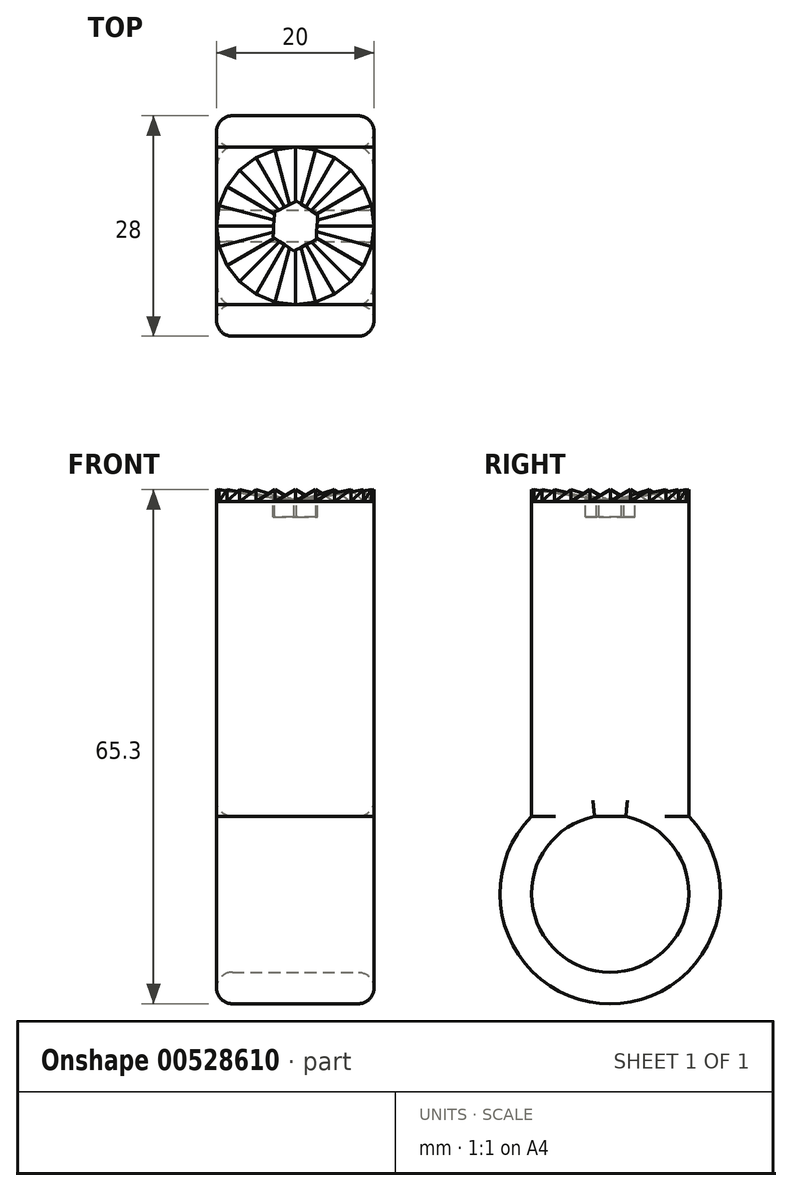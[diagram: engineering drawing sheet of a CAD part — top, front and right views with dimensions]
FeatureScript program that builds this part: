
annotation { "Feature Type Name" : "Feature", "Feature Type Description" : "" }
export const myFeature = defineFeature(function(context is Context, id is Id, definition is map)
    precondition{}
    {
        {
            var Q0;
            Q0=qCreatedBy(makeId("Top.planeOp"),FACE);
            var sketch = newSketch(context, id + "F0", { "sketchPlane" : qUnion([Q0])});
            skCircle(sketch, "E0", {"center": v(0, 0) * mm, "radius": 10 * mm});
            skLineSegment(sketch, "E1", {"start": v(0, 0) * mm, "end": v(0, 10) * mm});
            skLineSegment(sketch, "E2", {"start": v(0, 0) * mm, "end": v(2.59, 9.66) * mm});
            skLineSegment(sketch, "E3", {"start": v(0, 10) * mm, "end": v(2.59, 9.66) * mm});
            skCircle(sketch, "E4", {"center": v(0, 0) * mm, "radius": 1.5 * mm});
            skSolve(sketch);
        }
        {
            var Q0;
            Q0=sQuery(id+"F0.wireOp",EDGE,"E3");
            cPlane(context, id + "F1", {"entities" : qUnion([Q0]), "cplaneType" : CPlaneType.LINE_ANGLE, "offset" : 25 * mm, "angle" : 0 * degree, "width" : 150 * mm, "height" : 150 * mm});
        }
        {
            var Q0;
            Q0=qCreatedBy(id+"F1.planeOp",FACE);
            var sketch = newSketch(context, id + "F2", { "sketchPlane" : qUnion([Q0])});
            skLineSegment(sketch, "E5", {"start": v(1.3, 0) * mm, "end": v(1.3, 1.5) * mm});
            skLineSegment(sketch, "E6", {"start": v(1.3, 1.5) * mm, "end": v(-1.3, 0) * mm});
            skLineSegment(sketch, "E7", {"start": v(-1.3, 0) * mm, "end": v(1.3, 0) * mm});
            skLineSegment(sketch, "E8", {"start": v(-1.3, 0) * mm, "end": v(-1.3, 1.5) * mm});
            skLineSegment(sketch, "E9", {"start": v(-1.3, 1.5) * mm, "end": v(1.3, 1.5) * mm});
            skSolve(sketch);
        }
        {
            var Q0;
            Q0=makeQuery(id+"F2.imprint","IMPRINT",FACE,{"disambiguationData":[TD([[makeQuery(id+"F2.imprint","IMPRINT",EDGE,{"derivedFrom":sQuery(id+"F2.wireOp",EDGE,"E5")}),1.0]])]});
            var Q1;
            Q1=sQuery(id+"F0.wireOp",VERTEX,"E0.center");
            loft(context, id + "F3", {"sheetProfilesArray" : [{ "sheetProfileEntities" : qUnion([Q0]) }, { "sheetProfileEntities" : qUnion([Q1]) }]});
        }
        {
            var Q0;
            Q0=qCreatedBy(makeId("Right.planeOp"),FACE);
            var sketch = newSketch(context, id + "F4", { "sketchPlane" : qUnion([Q0])});
            skLineSegment(sketch, "E10", {"start": v(0, -4.83) * mm, "end": v(0, 8.7) * mm, "construction": true});
            skSolve(sketch);
        }
        {
            var Q0;
            Q0=makeQuery(id+"F3.opLoft","SWEPT_BODY",BODY,{"disambiguationData":[OSD([sQuery(id+"F0.wireOp",VERTEX,"E0.center"),makeQuery(id+"F2.imprint","IMPRINT",FACE,{"disambiguationData":[TD([[makeQuery(id+"F2.imprint","IMPRINT",EDGE,{"derivedFrom":sQuery(id+"F2.wireOp",EDGE,"E5")}),1.0]])]})])]});
            var Q1;
            Q1=sQuery(id+"F4.wireOp",EDGE,"E10");
            circularPattern(context, id + "F5", {"entities" : qUnion([Q0]), "axis" : qUnion([Q1]), "angle" : 360 * degree, "instanceCount" : 24, "equalSpace" : true});
        }
        {
            var Q0;
            Q0=qCreatedBy(makeId("Right.planeOp"),FACE);
            var sketch = newSketch(context, id + "F6", { "sketchPlane" : qUnion([Q0])});
            skLineSegment(sketch, "E11", {"start": v(0, 0) * mm, "end": v(-10, 0) * mm, "construction": true});
            skLineSegment(sketch, "E12.bottom", {"start": v(-10, 0) * mm, "end": v(10, 0) * mm});
            skLineSegment(sketch, "E12.top", {"start": v(-10, -40) * mm, "end": v(10, -40) * mm});
            skLineSegment(sketch, "E12.left", {"start": v(-10, 0) * mm, "end": v(-10, -40) * mm});
            skLineSegment(sketch, "E12.right", {"start": v(10, 0) * mm, "end": v(10, -40) * mm});
            skSolve(sketch);
        }
        {
            var Q0;
            Q0=makeQuery(id+"F6.imprint","IMPRINT",FACE,{"disambiguationData":[TD([[makeQuery(id+"F6.imprint","IMPRINT",EDGE,{"derivedFrom":sQuery(id+"F6.wireOp",EDGE,"E12.bottom")}),-1.0]])]});
            extrude(context, id + "F7", {"entities" : qUnion([Q0]), "depth" : 10 * mm, "offsetDistance" : 25 * mm, "hasSecondDirection" : true, "secondDirectionOppositeDirection" : true, "secondDirectionDepth" : 10 * mm});
        }
        {
            var Q0;
            Q0=makeQuery(id+"F7.opExtrude","SWEPT_FACE",FACE,{"disambiguationData":[OSD([sQuery(id+"F6.wireOp",EDGE,"E12.bottom")])]});
            var sketch = newSketch(context, id + "F8", { "sketchPlane" : qUnion([Q0])});
            skCircle(sketch, "E13.cCircle", {"center": v(0, 0) * mm, "radius": 2.75 * mm, "construction": true});
            skLineSegment(sketch, "E13.0", {"start": v(-2.65, 1.74) * mm, "end": v(0.18, 3.17) * mm});
            skLineSegment(sketch, "E13.1", {"start": v(0.18, 3.17) * mm, "end": v(2.84, 1.43) * mm});
            skLineSegment(sketch, "E13.2", {"start": v(2.84, 1.43) * mm, "end": v(2.65, -1.74) * mm});
            skLineSegment(sketch, "E13.3", {"start": v(2.65, -1.74) * mm, "end": v(-0.18, -3.17) * mm});
            skLineSegment(sketch, "E13.4", {"start": v(-0.18, -3.17) * mm, "end": v(-2.84, -1.43) * mm});
            skLineSegment(sketch, "E13.5", {"start": v(-2.84, -1.43) * mm, "end": v(-2.65, 1.74) * mm});
            skPoint(sketch, "E13.0.midPoint", {"position": v(-1.24, 2.46) * mm});
            skSolve(sketch);
        }
        {
            var Q0;
            Q0 = qSketchRegion(id + "F8", true);
            extrude(context, id + "F9", {"entities" : qUnion([Q0]), "operationType" : NewBodyOperationType.REMOVE, "oppositeDirection" : true, "depth" : 2 * mm, "offsetDistance" : 25 * mm, "hasSecondDirection" : true, "secondDirectionOppositeDirection" : false, "secondDirectionDepth" : 2 * mm});
        }
        {
            var Q0;
            Q0=makeQuery(id+"F7.opExtrude","CAP_FACE",FACE,{"disambiguationData":[OSD([sQuery(id+"F6.wireOp",EDGE,"E12.bottom"),sQuery(id+"F6.wireOp",EDGE,"E12.top"),sQuery(id+"F6.wireOp",EDGE,"E12.left"),sQuery(id+"F6.wireOp",EDGE,"E12.right")])],"isStart":false});
            var sketch = newSketch(context, id + "F10", { "sketchPlane" : qUnion([Q0])});
            skCircle(sketch, "E14", {"center": v(0, -49.8) * mm, "radius": 10 * mm});
            skPoint(sketch, "E14.first.point", {"position": v(-10, -49.8) * mm});
            skPoint(sketch, "E14.second.point", {"position": v(10, -49.8) * mm});
            skPoint(sketch, "E14.third.point", {"position": v(0, -59.8) * mm});
            skCircle(sketch, "E15.0", {"center": v(0, -49.8) * mm, "radius": 14 * mm});
            skSolve(sketch);
        }
        {
            var Q0;
            {var subQ0=sQuery(id+"F10.wireOp",EDGE,"E14");var subQ1=makeQuery(id+"F7.opExtrude","CAP_EDGE",EDGE,{"disambiguationData":[OSD([sQuery(id+"F6.wireOp",EDGE,"E12.top")])],"isStart":false});var subQ2=makeQuery(id+"F10.imprint","INTERSECT",VERTEX,{"disambiguationData":[OD(0.0)],"derivedFrom":[subQ1,subQ0]});Q0=makeQuery(id+"F10.imprint","IMPRINT",FACE,{"disambiguationData":[TD([[makeQuery(id+"F10.imprint","IMPRINT",EDGE,{"disambiguationData":[TD([[subQ2,-1.0]])],"derivedFrom":subQ0}),-1.0]])]});}
            extrude(context, id + "F11", {"entities" : qUnion([Q0]), "operationType" : NewBodyOperationType.ADD, "oppositeDirection" : true, "depth" : 20 * mm, "offsetDistance" : 25 * mm});
        }
        {
            var Q0;
            Q0=makeQuery(id+"F11.opExtrude","CAP_EDGE",EDGE,{"disambiguationData":[OSD([sQuery(id+"F10.wireOp",EDGE,"E14")])],"isStart":true});
            var Q1;
            {var subQ0=sQuery(id+"F6.wireOp",EDGE,"E12.top");var subQ1=sQuery(id+"F10.wireOp",EDGE,"E14");Q1=makeQuery(id+"F11.boolean.opBoolean","SPLIT",EDGE,{"disambiguationData":[TD([makeQuery(id+"F11.opExtrude","SWEPT_FACE",FACE,{"disambiguationData":[OSD([subQ1])]})])],"derivedFrom":makeQuery(id+"F7.opExtrude","CAP_EDGE",EDGE,{"disambiguationData":[OSD([subQ0])],"isStart":false})});}
            var Q2;
            {var subQ0=sQuery(id+"F6.wireOp",EDGE,"E12.top");var subQ1=sQuery(id+"F10.wireOp",EDGE,"E14");Q2=makeQuery(id+"F11.boolean.opBoolean","SPLIT",EDGE,{"disambiguationData":[TD([makeQuery(id+"F11.opExtrude","SWEPT_FACE",FACE,{"disambiguationData":[OSD([subQ1])]})])],"derivedFrom":makeQuery(id+"F7.opExtrude","CAP_EDGE",EDGE,{"disambiguationData":[OSD([subQ0])],"isStart":true})});}
            var Q3;
            Q3=makeQuery(id+"F11.opExtrude","CAP_EDGE",EDGE,{"disambiguationData":[OSD([sQuery(id+"F10.wireOp",EDGE,"E14")])],"isStart":false});
            var Q4;
            Q4=makeQuery(id+"F11.opExtrude","CAP_EDGE",EDGE,{"disambiguationData":[OSD([sQuery(id+"F10.wireOp",EDGE,"E15.0")])],"isStart":true});
            var Q5;
            Q5=makeQuery(id+"F11.opExtrude","CAP_EDGE",EDGE,{"disambiguationData":[OSD([sQuery(id+"F10.wireOp",EDGE,"E15.0")])],"isStart":false});
            fillet(context, id + "F12", {"entities" : qUnion([Q0, Q1, Q2, Q3, Q4, Q5]), "radius" : 2 * mm, "tangentPropagation" : true, "allowEdgeOverflow" : false});
        }
    });
